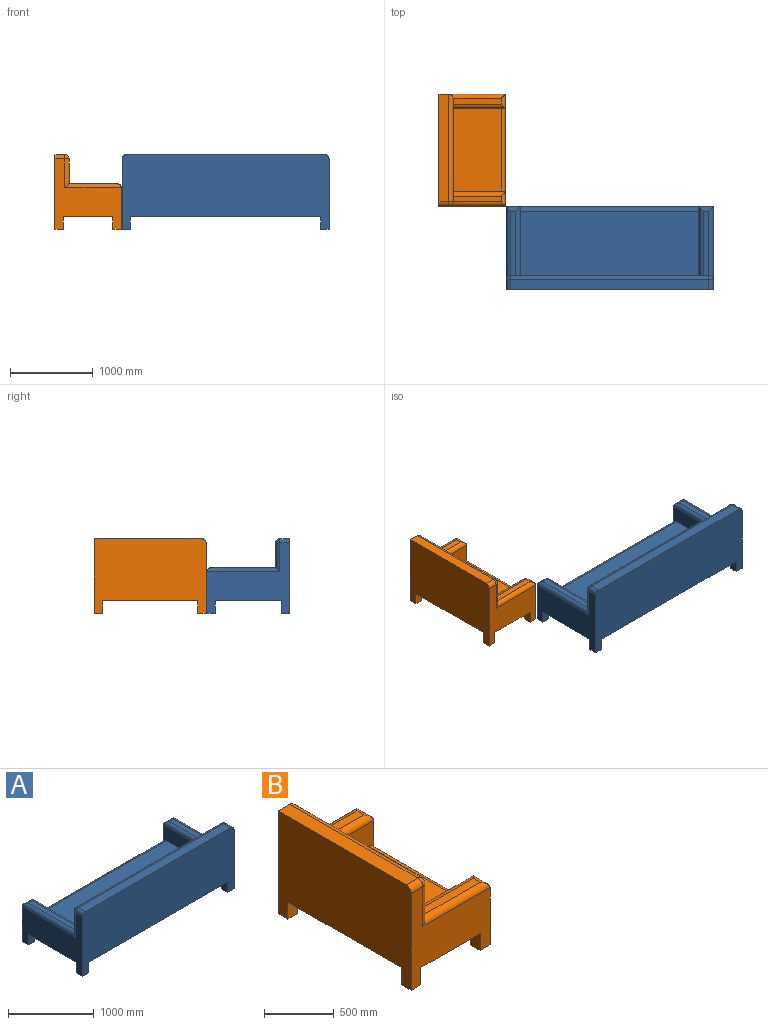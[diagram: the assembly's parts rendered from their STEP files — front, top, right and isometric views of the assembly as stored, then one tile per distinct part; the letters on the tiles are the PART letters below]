
ASSEMBLY  parts=2 mates=1
PART A: 38 faces, bbox 2500x1000x900 mm
  f0: plane 2160x780mm, normal (0,0,1), area 1684800mm2, adj f1,f8,f10,f25
  f1: plane 2400x550mm, normal (0,1,0), area 1261073mm2, adj f0,f8,f9,f10,f11,f12,f16,f19
  f2: plane 1000x850mm, normal (1,0,0), area 422000mm2, adj f3,f5,f6,f18,f21,f22,f27,f28
  f3: plane 2500x500mm, normal (0,1,0), area 365000mm2, adj f2,f4,f6,f8,f10,f13,f23,f25
  f4: plane 1000x850mm, normal (-1,0,0), area 422000mm2, adj f3,f5,f6,f14,f15,f16,f30,f31
  f5: plane 2500x900mm, normal (0,-1,0), area 1903927mm2, adj f2,f4,f6,f7,f15,f18,f32,f34
  f6: plane 2500x1000mm, normal (0,0,-1), area 2460000mm2, adj f2,f3,f4,f5,f26,f27,f29,f30
  f7: plane 2400x120mm, normal (0,0,1), area 288000mm2, adj f5,f15,f18,f19
  f8: plane 830x250mm, normal (-1,0,0), area 166536.5mm2, adj f0,f1,f3,f24,f25
  f9: plane 780x70mm, normal (0,0,1), area 54600mm2, adj f1,f22,f23,f24
  f10: plane 830x250mm, normal (1,0,0), area 166536.5mm2, adj f0,f1,f3,f12,f25
  f11: plane 780x70mm, normal (0,0,1), area 54600mm2, adj f1,f12,f13,f14
  f12: cylinder r=50mm len=830mm, axis (0,-1,0), area 63761.1mm2, adj f1,f10,f11,f13
  f13: cylinder r=50mm len=170mm, axis (1,0,0), area 10497.8mm2, adj f3,f11,f12,f14
  f14: cylinder r=50mm len=880mm, axis (0,1,0), area 65188mm2, adj f4,f11,f13,f16
  f15: cylinder r=50mm len=120mm, axis (0,1,0), area 9424.8mm2, adj f4,f5,f7,f17
  f16: cylinder r=50mm len=350mm, axis (0,0,-1), area 24988.9mm2, adj f1,f4,f14,f17
  f17: sphere r=50mm, area 3927mm2, adj f15,f16,f19
  f18: cylinder r=50mm len=120mm, axis (0,-1,0), area 9424.8mm2, adj f2,f5,f7,f20
  f19: cylinder r=50mm len=2400mm, axis (1,0,0), area 188495.6mm2, adj f1,f7,f17,f20
  f20: sphere r=50mm, area 3927mm2, adj f18,f19,f21
  f21: cylinder r=50mm len=350mm, axis (0,0,1), area 24988.9mm2, adj f1,f2,f20,f22
  f22: cylinder r=50mm len=880mm, axis (0,-1,0), area 65188mm2, adj f2,f9,f21,f23
  f23: cylinder r=50mm len=170mm, axis (1,0,0), area 10497.8mm2, adj f3,f9,f22,f24
  f24: cylinder r=50mm len=830mm, axis (0,1,0), area 63761.1mm2, adj f1,f8,f9,f23
  f25: cylinder r=50mm len=2160mm, axis (1,0,0), area 169646mm2, adj f0,f3,f8,f10
  f26: plane 150x100mm, normal (-1,0,0), area 15000mm2, adj f3,f6,f27,f28
  f27: plane 150x100mm, normal (0,-1,0), area 15000mm2, adj f2,f6,f26,f28
  f28: plane 100x100mm, normal (0,0,-1), area 10000mm2, adj f2,f3,f26,f27
  f29: plane 150x100mm, normal (1,0,0), area 15000mm2, adj f3,f6,f30,f31
  f30: plane 150x100mm, normal (0,-1,0), area 15000mm2, adj f4,f6,f29,f31
  f31: plane 100x100mm, normal (0,0,-1), area 10000mm2, adj f3,f4,f29,f30
  f32: plane 150x100mm, normal (-1,0,0), area 15000mm2, adj f5,f6,f33,f34
  f33: plane 150x100mm, normal (0,1,0), area 15000mm2, adj f2,f6,f32,f34
  f34: plane 100x100mm, normal (0,0,-1), area 10000mm2, adj f2,f5,f32,f33
  f35: plane 150x100mm, normal (0,1,0), area 15000mm2, adj f4,f6,f36,f37
  f36: plane 150x100mm, normal (1,0,0), area 15000mm2, adj f5,f6,f35,f37
  f37: plane 100x100mm, normal (0,0,-1), area 10000mm2, adj f4,f5,f35,f36
PART B: 36 faces, bbox 800x1350x900 mm
  f0: plane 1010x580mm, normal (0,0,1), area 585800mm2, adj f7,f9,f10,f23
  f1: plane 900x800mm, normal (0,1,0), area 358000mm2, adj f2,f3,f4,f11,f17,f20,f24,f25
  f2: plane 1350x800mm, normal (0,0,-1), area 1040000mm2, adj f1,f3,f4,f5,f25,f26,f28,f29
  f3: plane 1350x900mm, normal (-1,0,0), area 1041963.5mm2, adj f1,f2,f5,f11,f19,f24,f26,f27
  f4: plane 1350x500mm, normal (1,0,0), area 250000mm2, adj f1,f2,f5,f7,f9,f14,f15,f23
  f5: plane 850x800mm, normal (0,-1,0), area 352000mm2, adj f2,f3,f4,f16,f18,f19,f27,f29
  f6: plane 580x70mm, normal (0,0,1), area 40600mm2, adj f10,f12,f14,f16
  f7: plane 630x250mm, normal (0,1,0), area 126536.5mm2, adj f0,f4,f10,f12,f23
  f8: plane 580x70mm, normal (0,0,1), area 40600mm2, adj f10,f13,f15,f17
  f9: plane 630x250mm, normal (0,-1,0), area 126536.5mm2, adj f0,f4,f10,f13,f23
  f10: plane 1250x550mm, normal (1,0,0), area 628573mm2, adj f0,f6,f7,f8,f9,f12,f13,f18
  f11: plane 1300x120mm, normal (0,0,1), area 156000mm2, adj f1,f3,f19,f22
  f12: cylinder r=50mm len=630mm, axis (1,0,0), area 48053.1mm2, adj f6,f7,f10,f14
  f13: cylinder r=50mm len=630mm, axis (-1,0,0), area 48053.1mm2, adj f8,f9,f10,f15
  f14: cylinder r=50mm len=170mm, axis (0,-1,0), area 10497.8mm2, adj f4,f6,f12,f16
  f15: cylinder r=50mm len=170mm, axis (0,-1,0), area 10497.8mm2, adj f4,f8,f13,f17
  f16: cylinder r=50mm len=680mm, axis (-1,0,0), area 49480.1mm2, adj f5,f6,f14,f18
  f17: cylinder r=50mm len=680mm, axis (1,0,0), area 49480.1mm2, adj f1,f8,f15,f20
  f18: cylinder r=50mm len=350mm, axis (0,0,-1), area 24988.9mm2, adj f5,f10,f16,f21
  f19: cylinder r=50mm len=120mm, axis (-1,0,0), area 9424.8mm2, adj f3,f5,f11,f21
  f20: cylinder r=50mm len=400mm, axis (0,0,1), area 27488.9mm2, adj f1,f10,f17,f22
  f21: sphere r=50mm, area 3927mm2, adj f18,f19,f22
  f22: cylinder r=50mm len=1300mm, axis (0,-1,0), area 100674.8mm2, adj f10,f11,f20,f21
  f23: cylinder r=50mm len=1010mm, axis (0,-1,0), area 79325.2mm2, adj f0,f4,f7,f9
  f24: plane 100x100mm, normal (0,0,-1), area 10000mm2, adj f1,f3,f25,f26
  f25: plane 150x100mm, normal (1,0,0), area 15000mm2, adj f1,f2,f24,f26
  f26: plane 150x100mm, normal (0,-1,0), area 15000mm2, adj f2,f3,f24,f25
  f27: plane 100x100mm, normal (0,0,-1), area 10000mm2, adj f3,f5,f28,f29
  f28: plane 150x100mm, normal (0,1,0), area 15000mm2, adj f2,f3,f27,f29
  f29: plane 150x100mm, normal (1,0,0), area 15000mm2, adj f2,f5,f27,f28
  f30: plane 100x100mm, normal (0,0,-1), area 10000mm2, adj f4,f5,f31,f32
  f31: plane 150x100mm, normal (-1,0,0), area 15000mm2, adj f2,f5,f30,f32
  f32: plane 150x100mm, normal (0,1,0), area 15000mm2, adj f2,f4,f30,f31
  f33: plane 100x100mm, normal (0,0,-1), area 10000mm2, adj f1,f4,f34,f35
  f34: plane 150x100mm, normal (-1,0,0), area 15000mm2, adj f1,f2,f33,f35
  f35: plane 150x100mm, normal (0,-1,0), area 15000mm2, adj f2,f4,f33,f34
PLACE A t=(-1817.79,965.21,-188.87)mm fixed
PLACE B t=(-1817.79,965.21,-188.87)mm
MATE fastened A.f31 <-> B.f30  axis (0,0,-1) through (-3067.79,1465.21,-338.87)mm
